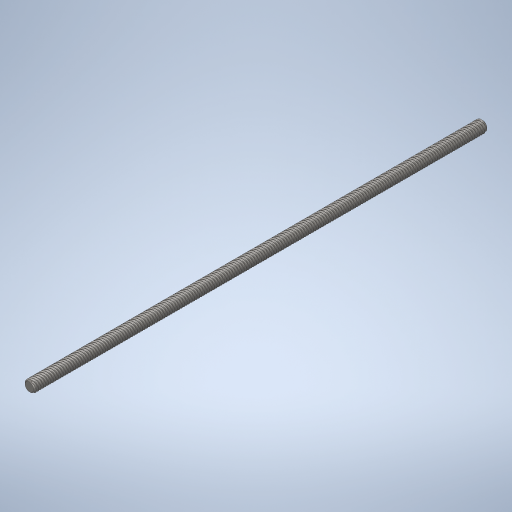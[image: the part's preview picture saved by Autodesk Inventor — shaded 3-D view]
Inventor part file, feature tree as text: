
AUTODESK INVENTOR PART (.ipt)
format: ipt  version: 2024.2 (Build 282272000, 272)  size: 822,784 bytes
history: native  units: mm
features: helix x2, extrude x1, sketch x1, chamfer x1
ambient origin geometry x8: Origin, YZ Plane, XZ Plane, XY Plane, X Axis, Y Axis, Z Axis, Center Point
bodies: Solid1 (feature_tree)
feature tree (5):
  extrude  "Extrusion1"  Depth=10.0mm TaperAngle=0.0deg
  sketch  "Sketch2"  dims[d0=8.0mm d1=320.0mm d2=0.0mm d3=1.4mm d4=4.0mm d13=1.0mm d14=2.0mm d15=45.0deg d16=1.4mm d17=1.4mm d18=1.4mm d19=7.0mm d20=10.0mm d21=2000.0mm d22=0.0mm d23=90.0deg d24=90.0deg d25=0.0mm d26=0.0mm d35=7.0mm d36=10.0mm d37=2000.0mm d38=0.0mm d39=90.0deg d40=90.0deg d41=0.0mm d42=0.0mm]
  chamfer  "Chamfer1"  Distance=1.4mm
  helix  "Coil2"  [1 undecoded]
  helix  "Coil4"  [1 undecoded]
note: 2 required parameter values undecoded (feature->parameter linkage not recoverable at this tier; creation-order binding heuristic only, values carry confidence <= 0.55)
